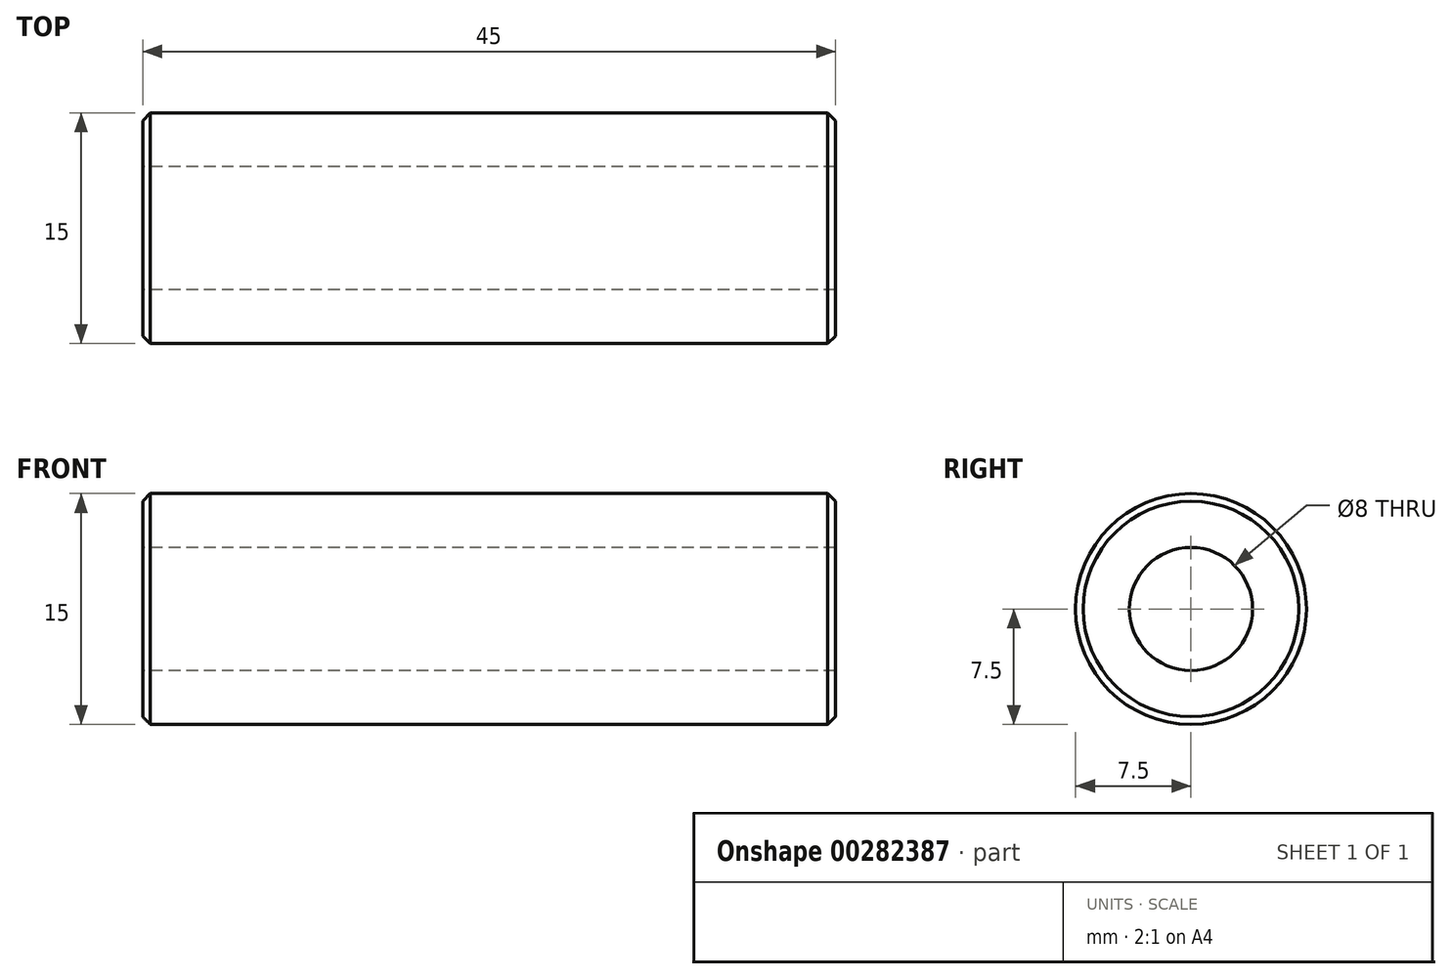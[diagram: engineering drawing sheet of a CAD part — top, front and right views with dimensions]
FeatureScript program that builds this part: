
annotation { "Feature Type Name" : "Feature", "Feature Type Description" : "" }
export const myFeature = defineFeature(function(context is Context, id is Id, definition is map)
    precondition{}
    {
        {
            var Q0;
            Q0=qCreatedBy(makeId("Right.planeOp"),FACE);
            var sketch = newSketch(context, id + "F0", { "sketchPlane" : qUnion([Q0])});
            skCircle(sketch, "E0", {"center": v(0, 0) * mm, "radius": 4 * mm});
            skCircle(sketch, "E1", {"center": v(0, 0) * mm, "radius": 7.5 * mm});
            skSolve(sketch);
        }
        {
            var Q0;
            Q0=qSketchRegion(id+"F0",true);
            extrude(context, id + "F1", {"entities" : qUnion([Q0]), "depth" : 45 * mm});
        }
        {
            var Q0;
            Q0=makeQuery(id+"F1.opExtrude","CAP_EDGE",EDGE,{"disambiguationData":[OSD([sQuery(id+"F0.wireOp",EDGE,"E1")])],"isStart":true});
            var Q1;
            Q1=makeQuery(id+"F1.opExtrude","CAP_EDGE",EDGE,{"disambiguationData":[OSD([sQuery(id+"F0.wireOp",EDGE,"E1")])],"isStart":false});
            chamfer(context, id + "F2", {"entities" : qUnion([Q0, Q1]), "width" : 0.5 * mm, "tangentPropagation" : true});
        }
    });
